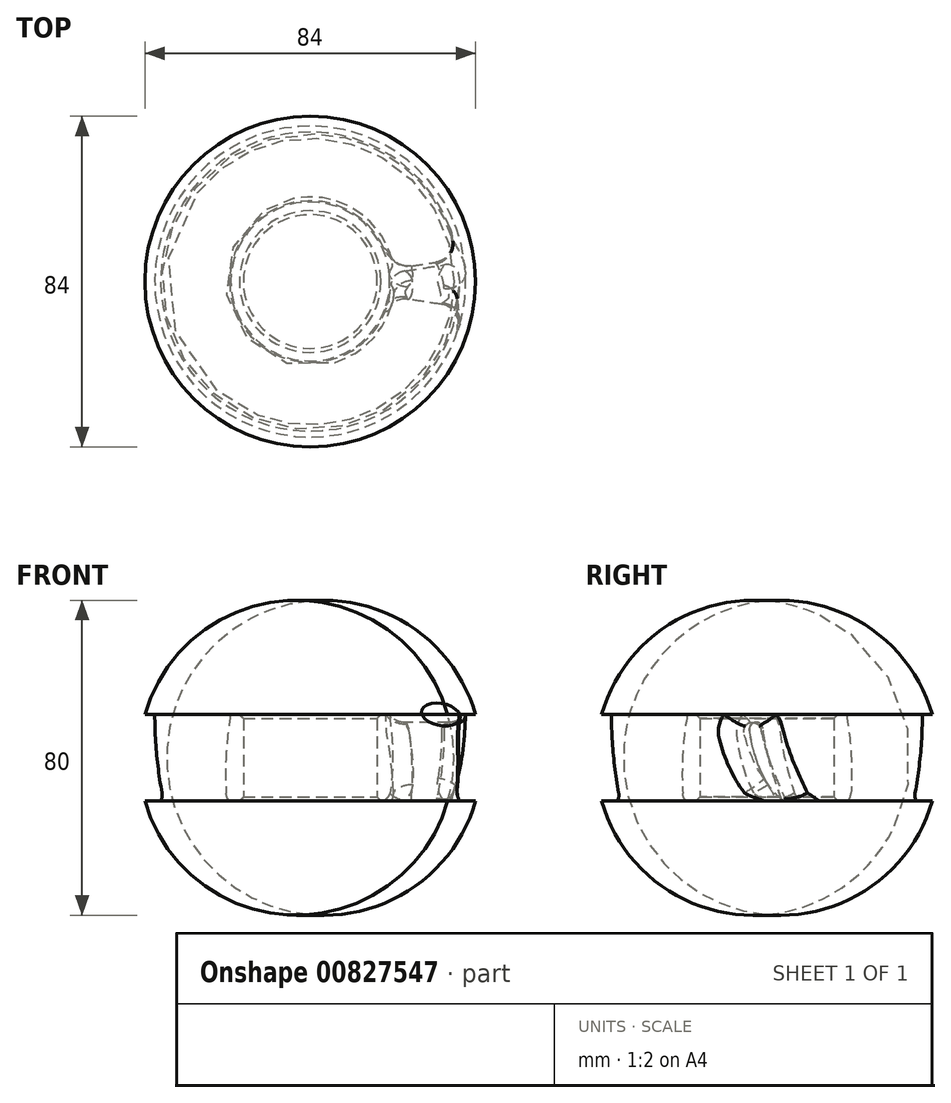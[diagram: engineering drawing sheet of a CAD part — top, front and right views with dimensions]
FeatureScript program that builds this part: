
annotation { "Feature Type Name" : "Feature", "Feature Type Description" : "" }
export const myFeature = defineFeature(function(context is Context, id is Id, definition is map)
    precondition{}
    {
        {
            var Q0;
            Q0=qCreatedBy(makeId("Right.planeOp"),FACE);
            cPlane(context, id + "F0", {"entities" : qUnion([Q0]), "cplaneType" : CPlaneType.OFFSET, "offset" : 20 * mm, "width" : 152.4 * mm, "height" : 152.4 * mm});
        }
        {
            var Q0;
            Q0=qCreatedBy(id+"F0.planeOp",FACE);
            cPlane(context, id + "F1", {"entities" : qUnion([Q0]), "cplaneType" : CPlaneType.OFFSET, "offset" : 10 * mm, "width" : 150 * mm, "height" : 150 * mm});
        }
        {
            var Q0;
            Q0=qCreatedBy(id+"F1.planeOp",FACE);
            cPlane(context, id + "F2", {"entities" : qUnion([Q0]), "cplaneType" : CPlaneType.OFFSET, "offset" : 10 * mm, "width" : 150 * mm, "height" : 150 * mm});
        }
        {
            var Q0;
            Q0=qCreatedBy(makeId("Right.planeOp"),FACE);
            var sketch = newSketch(context, id + "F3", { "sketchPlane" : qUnion([Q0])});
            skLineSegment(sketch, "E0.bottom", {"start": v(-22.5, 10) * mm, "end": v(22.5, 10) * mm});
            skLineSegment(sketch, "E0.top", {"start": v(-22.5, -10) * mm, "end": v(22.5, -10) * mm});
            skLineSegment(sketch, "E0.left", {"start": v(-22.5, 10) * mm, "end": v(-22.5, -10) * mm});
            skLineSegment(sketch, "E0.right", {"start": v(22.5, 10) * mm, "end": v(22.5, -10) * mm});
            skLineSegment(sketch, "E1", {"start": v(0, 10) * mm, "end": v(0, -10) * mm, "construction": true});
            skLineSegment(sketch, "E2", {"start": v(-22.5, 0) * mm, "end": v(22.5, 0) * mm, "construction": true});
            skSolve(sketch);
        }
        {
            var Q0;
            Q0=qCreatedBy(id+"F0.planeOp",FACE);
            var sketch = newSketch(context, id + "F4", { "sketchPlane" : qUnion([Q0])});
            skArc(sketch, "E3", {"start": v(-0.72, 8.68) * mm, "mid": v(-2.39, 9.99) * mm, "end": v(-3.7, 8.32) * mm});
            skArc(sketch, "E4", {"start": v(-0.72, 8.68) * mm, "mid": v(0.82, -0.73) * mm, "end": v(3.1, -10) * mm});
            skArc(sketch, "E5", {"start": v(-3.7, 8.32) * mm, "mid": v(-1.64, -1.1) * mm, "end": v(2.1, -10) * mm});
            skLineSegment(sketch, "E6", {"start": v(-3.7, 8.32) * mm, "end": v(-0.72, 8.68) * mm, "construction": true});
            skLineSegment(sketch, "E7", {"start": v(2.1, -10) * mm, "end": v(3.1, -10) * mm});
            skLineSegment(sketch, "E8", {"start": v(-2.2, 8.5) * mm, "end": v(2.6, -10) * mm, "construction": true});
            skLineSegment(sketch, "E9", {"start": v(48.43, 14.72) * mm, "end": v(2.1, -10) * mm, "construction": true});
            skLineSegment(sketch, "E10", {"start": v(119.1, 23.4) * mm, "end": v(3.1, -10) * mm, "construction": true});
            skSolve(sketch);
        }
        {
            var Q0;
            Q0=qCreatedBy(id+"F1.planeOp",FACE);
            var sketch = newSketch(context, id + "F5", { "sketchPlane" : qUnion([Q0])});
            skArc(sketch, "E11", {"start": v(-1.32, 8.36) * mm, "mid": v(-3.65, 9.97) * mm, "end": v(-5.26, 7.64) * mm});
            skArc(sketch, "E12", {"start": v(-5.26, 7.64) * mm, "mid": v(-2.08, -1.81) * mm, "end": v(3.61, -10) * mm});
            skArc(sketch, "E13", {"start": v(-1.32, 8.36) * mm, "mid": v(1.05, -1) * mm, "end": v(4.61, -10) * mm});
            skLineSegment(sketch, "E14", {"start": v(-3.29, 8) * mm, "end": v(4.11, -10) * mm, "construction": true});
            skLineSegment(sketch, "E15", {"start": v(-5.26, 7.64) * mm, "end": v(-1.32, 8.36) * mm, "construction": true});
            skLineSegment(sketch, "E16", {"start": v(3.61, -10) * mm, "end": v(4.61, -10) * mm});
            skLineSegment(sketch, "E17", {"start": v(29.55, 14.09) * mm, "end": v(3.61, -10) * mm, "construction": true});
            skLineSegment(sketch, "E18", {"start": v(72.3, 22) * mm, "end": v(4.61, -10) * mm, "construction": true});
            skSolve(sketch);
        }
        {
            var Q0;
            Q0=qCreatedBy(id+"F2.planeOp",FACE);
            var sketch = newSketch(context, id + "F6", { "sketchPlane" : qUnion([Q0])});
            skArc(sketch, "E19", {"start": v(-1.86, 8.1) * mm, "mid": v(-4.9, 9.93) * mm, "end": v(-6.71, 6.9) * mm});
            skArc(sketch, "E20", {"start": v(-6.71, 6.9) * mm, "mid": v(-2.33, -2.67) * mm, "end": v(5.21, -10) * mm});
            skArc(sketch, "E21", {"start": v(-1.86, 8.1) * mm, "mid": v(1.38, -1.3) * mm, "end": v(6.21, -10) * mm});
            skLineSegment(sketch, "E22", {"start": v(5.21, -10) * mm, "end": v(6.21, -10) * mm});
            skLineSegment(sketch, "E23", {"start": v(-6.71, 6.9) * mm, "end": v(-1.86, 8.1) * mm, "construction": true});
            skLineSegment(sketch, "E24", {"start": v(21.01, 13.8) * mm, "end": v(5.21, -10) * mm, "construction": true});
            skLineSegment(sketch, "E25", {"start": v(-4.29, 7.5) * mm, "end": v(5.71, -10) * mm, "construction": true});
            skLineSegment(sketch, "E26", {"start": v(6.21, -10) * mm, "end": v(53.33, 21.87) * mm, "construction": true});
            skSolve(sketch);
        }
        {
            var Q0;
            Q0 = qSketchRegion(id + "F4", true);
            var Q1;
            Q1 = qSketchRegion(id + "F5", true);
            var Q2;
            Q2 = qSketchRegion(id + "F6", true);
            loft(context, id + "F7", {"sheetProfilesArray" : [{ "sheetProfileEntities" : qUnion([Q0]) }, { "sheetProfileEntities" : qUnion([Q1]) }, { "sheetProfileEntities" : qUnion([Q2]) }]});
        }
        {
            var Q0;
            Q0=qCreatedBy(makeId("Front.planeOp"),FACE);
            var sketch = newSketch(context, id + "F8", { "sketchPlane" : qUnion([Q0])});
            skLineSegment(sketch, "E27", {"start": v(0, 0) * mm, "end": v(0, 20) * mm, "construction": true});
            skLineSegment(sketch, "E28", {"start": v(17, -10) * mm, "end": v(17, 11.99) * mm});
            skLineSegment(sketch, "E29", {"start": v(17, 11.99) * mm, "end": v(20.2, 11.99) * mm});
            skLineSegment(sketch, "E30", {"start": v(20.5, -10) * mm, "end": v(17, -10) * mm});
            skLineSegment(sketch, "E31", {"start": v(42, 11.99) * mm, "end": v(42, -10) * mm, "construction": true});
            skLineSegment(sketch, "E32", {"start": v(42, -10) * mm, "end": v(38, -10) * mm});
            skLineSegment(sketch, "E33", {"start": v(39.5, 11.99) * mm, "end": v(42, 11.99) * mm});
            skArc(sketch, "E34", {"start": v(42, -10) * mm, "mid": v(43.54, 1) * mm, "end": v(42, 11.99) * mm});
            skArc(sketch, "E35", {"start": v(20.5, -10) * mm, "mid": v(21.12, -9.1) * mm, "end": v(21.37, -8.05) * mm});
            skArc(sketch, "E36", {"start": v(20.2, 11.99) * mm, "mid": v(21.37, 2) * mm, "end": v(21.37, -8.05) * mm});
            skLineSegment(sketch, "E37", {"start": v(18.38, -7.88) * mm, "end": v(20.5, -10) * mm, "construction": true});
            skArc(sketch, "E38", {"start": v(37.65, -7.95) * mm, "mid": v(39.04, 1.98) * mm, "end": v(39.5, 11.99) * mm});
            skArc(sketch, "E39", {"start": v(37.65, -7.95) * mm, "mid": v(37.64, -9) * mm, "end": v(38, -10) * mm});
            skLineSegment(sketch, "E40", {"start": v(40.6, -8.5) * mm, "end": v(38, -10) * mm, "construction": true});
            skLineSegment(sketch, "E41", {"start": v(-65.18, -3.07) * mm, "end": v(20.2, 11.99) * mm, "construction": true});
            skSolve(sketch);
        }
        {
            var Q0;
            Q0=makeQuery(id+"F8.imprint","IMPRINT",FACE,{"disambiguationData":[TD([[makeQuery(id+"F8.imprint","IMPRINT",EDGE,{"derivedFrom":sQuery(id+"F8.wireOp",EDGE,"E28")}),-1.0]])]});
            var Q1;
            Q1=sQuery(id+"F8.wireOp",EDGE,"E27");
            revolve(context, id + "F9", {"operationType" : NewBodyOperationType.ADD, "surfaceOperationType" : NewSurfaceOperationType.NEW, "entities" : qUnion([Q0]), "axis" : qUnion([Q1]), "revolveType" : RevolveType.FULL});
        }
        {
            var Q0;
            Q0=makeQuery(id+"F8.imprint","IMPRINT",FACE,{"disambiguationData":[TD([[makeQuery(id+"F8.imprint","IMPRINT",EDGE,{"derivedFrom":sQuery(id+"F8.wireOp",EDGE,"E32")}),-1.0]])]});
            var Q1;
            Q1=sQuery(id+"F8.wireOp",EDGE,"E27");
            revolve(context, id + "F10", {"operationType" : NewBodyOperationType.ADD, "surfaceOperationType" : NewSurfaceOperationType.NEW, "entities" : qUnion([Q0]), "axis" : qUnion([Q1]), "revolveType" : RevolveType.FULL});
        }
        {
            var Q0;
            Q0=makeQuery(id+"F9.boolean.opBoolean","INTERSECT",EDGE,{"derivedFrom":[makeQuery(id+"F7.opLoft","SWEPT_FACE",FACE,{"disambiguationData":[OSD([sQuery(id+"F4.wireOp",EDGE,"E3"),sQuery(id+"F4.wireOp",EDGE,"E4"),sQuery(id+"F4.wireOp",EDGE,"E7"),sQuery(id+"F5.wireOp",EDGE,"E11"),sQuery(id+"F5.wireOp",EDGE,"E13"),sQuery(id+"F5.wireOp",EDGE,"E16")])]}),makeQuery(id+"F9.opRevolve","SWEPT_FACE",FACE,{"disambiguationData":[OSD([sQuery(id+"F8.wireOp",EDGE,"E36")])]})]});
            var Q1;
            Q1=makeQuery(id+"F9.boolean.opBoolean","INTERSECT",EDGE,{"derivedFrom":[makeQuery(id+"F53g4K2dghI7kLQ_1.1.F7.opLoft","SWEPT_FACE",FACE,{"disambiguationData":[OSD([sQuery(id+"F4.wireOp",EDGE,"E3"),sQuery(id+"F4.wireOp",EDGE,"E4"),sQuery(id+"F4.wireOp",EDGE,"E7"),sQuery(id+"F5.wireOp",EDGE,"E11"),sQuery(id+"F5.wireOp",EDGE,"E13"),sQuery(id+"F5.wireOp",EDGE,"E16")])]}),makeQuery(id+"F9.opRevolve","SWEPT_FACE",FACE,{"disambiguationData":[OSD([sQuery(id+"F8.wireOp",EDGE,"E36")])]})]});
            var Q2;
            Q2=makeQuery(id+"F9.boolean.opBoolean","INTERSECT",EDGE,{"derivedFrom":[makeQuery(id+"F53g4K2dghI7kLQ_1.2.F7.opLoft","SWEPT_FACE",FACE,{"disambiguationData":[OSD([sQuery(id+"F4.wireOp",EDGE,"E3"),sQuery(id+"F4.wireOp",EDGE,"E4"),sQuery(id+"F4.wireOp",EDGE,"E7"),sQuery(id+"F5.wireOp",EDGE,"E11"),sQuery(id+"F5.wireOp",EDGE,"E13"),sQuery(id+"F5.wireOp",EDGE,"E16")])]}),makeQuery(id+"F9.opRevolve","SWEPT_FACE",FACE,{"disambiguationData":[OSD([sQuery(id+"F8.wireOp",EDGE,"E36")])]})]});
            var Q3;
            Q3=makeQuery(id+"F9.boolean.opBoolean","INTERSECT",EDGE,{"derivedFrom":[makeQuery(id+"F53g4K2dghI7kLQ_1.3.F7.opLoft","SWEPT_FACE",FACE,{"disambiguationData":[OSD([sQuery(id+"F4.wireOp",EDGE,"E3"),sQuery(id+"F4.wireOp",EDGE,"E4"),sQuery(id+"F4.wireOp",EDGE,"E7"),sQuery(id+"F5.wireOp",EDGE,"E11"),sQuery(id+"F5.wireOp",EDGE,"E13"),sQuery(id+"F5.wireOp",EDGE,"E16")])]}),makeQuery(id+"F9.opRevolve","SWEPT_FACE",FACE,{"disambiguationData":[OSD([sQuery(id+"F8.wireOp",EDGE,"E36")])]})]});
            var Q4;
            Q4=makeQuery(id+"F9.boolean.opBoolean","INTERSECT",EDGE,{"derivedFrom":[makeQuery(id+"F53g4K2dghI7kLQ_1.4.F7.opLoft","SWEPT_FACE",FACE,{"disambiguationData":[OSD([sQuery(id+"F4.wireOp",EDGE,"E3"),sQuery(id+"F4.wireOp",EDGE,"E4"),sQuery(id+"F4.wireOp",EDGE,"E7"),sQuery(id+"F5.wireOp",EDGE,"E11"),sQuery(id+"F5.wireOp",EDGE,"E13"),sQuery(id+"F5.wireOp",EDGE,"E16")])]}),makeQuery(id+"F9.opRevolve","SWEPT_FACE",FACE,{"disambiguationData":[OSD([sQuery(id+"F8.wireOp",EDGE,"E36")])]})]});
            var Q5;
            Q5=makeQuery(id+"F9.boolean.opBoolean","INTERSECT",EDGE,{"derivedFrom":[makeQuery(id+"F53g4K2dghI7kLQ_1.5.F7.opLoft","SWEPT_FACE",FACE,{"disambiguationData":[OSD([sQuery(id+"F4.wireOp",EDGE,"E3"),sQuery(id+"F4.wireOp",EDGE,"E4"),sQuery(id+"F4.wireOp",EDGE,"E7"),sQuery(id+"F5.wireOp",EDGE,"E11"),sQuery(id+"F5.wireOp",EDGE,"E13"),sQuery(id+"F5.wireOp",EDGE,"E16")])]}),makeQuery(id+"F9.opRevolve","SWEPT_FACE",FACE,{"disambiguationData":[OSD([sQuery(id+"F8.wireOp",EDGE,"E36")])]})]});
            var Q6;
            Q6=makeQuery(id+"F9.boolean.opBoolean","INTERSECT",EDGE,{"derivedFrom":[makeQuery(id+"F53g4K2dghI7kLQ_1.6.F7.opLoft","SWEPT_FACE",FACE,{"disambiguationData":[OSD([sQuery(id+"F4.wireOp",EDGE,"E3"),sQuery(id+"F4.wireOp",EDGE,"E4"),sQuery(id+"F4.wireOp",EDGE,"E7"),sQuery(id+"F5.wireOp",EDGE,"E11"),sQuery(id+"F5.wireOp",EDGE,"E13"),sQuery(id+"F5.wireOp",EDGE,"E16")])]}),makeQuery(id+"F9.opRevolve","SWEPT_FACE",FACE,{"disambiguationData":[OSD([sQuery(id+"F8.wireOp",EDGE,"E36")])]})]});
            var Q7;
            Q7=makeQuery(id+"F9.boolean.opBoolean","INTERSECT",EDGE,{"derivedFrom":[makeQuery(id+"F53g4K2dghI7kLQ_1.7.F7.opLoft","SWEPT_FACE",FACE,{"disambiguationData":[OSD([sQuery(id+"F4.wireOp",EDGE,"E3"),sQuery(id+"F4.wireOp",EDGE,"E4"),sQuery(id+"F4.wireOp",EDGE,"E7"),sQuery(id+"F5.wireOp",EDGE,"E11"),sQuery(id+"F5.wireOp",EDGE,"E13"),sQuery(id+"F5.wireOp",EDGE,"E16")])]}),makeQuery(id+"F9.opRevolve","SWEPT_FACE",FACE,{"disambiguationData":[OSD([sQuery(id+"F8.wireOp",EDGE,"E36")])]})]});
            var Q8;
            Q8=makeQuery(id+"F9.boolean.opBoolean","INTERSECT",EDGE,{"derivedFrom":[makeQuery(id+"F53g4K2dghI7kLQ_1.8.F7.opLoft","SWEPT_FACE",FACE,{"disambiguationData":[OSD([sQuery(id+"F4.wireOp",EDGE,"E3"),sQuery(id+"F4.wireOp",EDGE,"E4"),sQuery(id+"F4.wireOp",EDGE,"E7"),sQuery(id+"F5.wireOp",EDGE,"E11"),sQuery(id+"F5.wireOp",EDGE,"E13"),sQuery(id+"F5.wireOp",EDGE,"E16")])]}),makeQuery(id+"F9.opRevolve","SWEPT_FACE",FACE,{"disambiguationData":[OSD([sQuery(id+"F8.wireOp",EDGE,"E36")])]})]});
            var Q9;
            Q9=makeQuery(id+"F9.boolean.opBoolean","INTERSECT",EDGE,{"derivedFrom":[makeQuery(id+"F53g4K2dghI7kLQ_1.9.F7.opLoft","SWEPT_FACE",FACE,{"disambiguationData":[OSD([sQuery(id+"F4.wireOp",EDGE,"E3"),sQuery(id+"F4.wireOp",EDGE,"E4"),sQuery(id+"F4.wireOp",EDGE,"E7"),sQuery(id+"F5.wireOp",EDGE,"E11"),sQuery(id+"F5.wireOp",EDGE,"E13"),sQuery(id+"F5.wireOp",EDGE,"E16")])]}),makeQuery(id+"F9.opRevolve","SWEPT_FACE",FACE,{"disambiguationData":[OSD([sQuery(id+"F8.wireOp",EDGE,"E36")])]})]});
            var Q10;
            Q10=makeQuery(id+"F9.boolean.opBoolean","INTERSECT",EDGE,{"derivedFrom":[makeQuery(id+"F53g4K2dghI7kLQ_1.10.F7.opLoft","SWEPT_FACE",FACE,{"disambiguationData":[OSD([sQuery(id+"F4.wireOp",EDGE,"E3"),sQuery(id+"F4.wireOp",EDGE,"E4"),sQuery(id+"F4.wireOp",EDGE,"E7"),sQuery(id+"F5.wireOp",EDGE,"E11"),sQuery(id+"F5.wireOp",EDGE,"E13"),sQuery(id+"F5.wireOp",EDGE,"E16")])]}),makeQuery(id+"F9.opRevolve","SWEPT_FACE",FACE,{"disambiguationData":[OSD([sQuery(id+"F8.wireOp",EDGE,"E36")])]})]});
            var Q11;
            Q11=makeQuery(id+"F9.boolean.opBoolean","INTERSECT",EDGE,{"derivedFrom":[makeQuery(id+"F53g4K2dghI7kLQ_1.11.F7.opLoft","SWEPT_FACE",FACE,{"disambiguationData":[OSD([sQuery(id+"F4.wireOp",EDGE,"E3"),sQuery(id+"F4.wireOp",EDGE,"E4"),sQuery(id+"F4.wireOp",EDGE,"E7"),sQuery(id+"F5.wireOp",EDGE,"E11"),sQuery(id+"F5.wireOp",EDGE,"E13"),sQuery(id+"F5.wireOp",EDGE,"E16")])]}),makeQuery(id+"F9.opRevolve","SWEPT_FACE",FACE,{"disambiguationData":[OSD([sQuery(id+"F8.wireOp",EDGE,"E36")])]})]});
            var Q12;
            Q12=makeQuery(id+"F9.boolean.opBoolean","INTERSECT",EDGE,{"derivedFrom":[makeQuery(id+"F53g4K2dghI7kLQ_1.12.F7.opLoft","SWEPT_FACE",FACE,{"disambiguationData":[OSD([sQuery(id+"F4.wireOp",EDGE,"E3"),sQuery(id+"F4.wireOp",EDGE,"E4"),sQuery(id+"F4.wireOp",EDGE,"E7"),sQuery(id+"F5.wireOp",EDGE,"E11"),sQuery(id+"F5.wireOp",EDGE,"E13"),sQuery(id+"F5.wireOp",EDGE,"E16")])]}),makeQuery(id+"F9.opRevolve","SWEPT_FACE",FACE,{"disambiguationData":[OSD([sQuery(id+"F8.wireOp",EDGE,"E36")])]})]});
            var Q13;
            Q13=makeQuery(id+"F9.boolean.opBoolean","INTERSECT",EDGE,{"derivedFrom":[makeQuery(id+"F53g4K2dghI7kLQ_1.13.F7.opLoft","SWEPT_FACE",FACE,{"disambiguationData":[OSD([sQuery(id+"F4.wireOp",EDGE,"E3"),sQuery(id+"F4.wireOp",EDGE,"E4"),sQuery(id+"F4.wireOp",EDGE,"E7"),sQuery(id+"F5.wireOp",EDGE,"E11"),sQuery(id+"F5.wireOp",EDGE,"E13"),sQuery(id+"F5.wireOp",EDGE,"E16")])]}),makeQuery(id+"F9.opRevolve","SWEPT_FACE",FACE,{"disambiguationData":[OSD([sQuery(id+"F8.wireOp",EDGE,"E36")])]})]});
            var Q14;
            Q14=makeQuery(id+"F9.boolean.opBoolean","INTERSECT",EDGE,{"derivedFrom":[makeQuery(id+"F53g4K2dghI7kLQ_1.14.F7.opLoft","SWEPT_FACE",FACE,{"disambiguationData":[OSD([sQuery(id+"F4.wireOp",EDGE,"E3"),sQuery(id+"F4.wireOp",EDGE,"E4"),sQuery(id+"F4.wireOp",EDGE,"E7"),sQuery(id+"F5.wireOp",EDGE,"E11"),sQuery(id+"F5.wireOp",EDGE,"E13"),sQuery(id+"F5.wireOp",EDGE,"E16")])]}),makeQuery(id+"F9.opRevolve","SWEPT_FACE",FACE,{"disambiguationData":[OSD([sQuery(id+"F8.wireOp",EDGE,"E36")])]})]});
            var Q15;
            Q15=makeQuery(id+"F10.boolean.opBoolean","INTERSECT",EDGE,{"derivedFrom":[makeQuery(id+"F7.opLoft","SWEPT_FACE",FACE,{"disambiguationData":[OSD([sQuery(id+"F4.wireOp",EDGE,"E3"),sQuery(id+"F4.wireOp",EDGE,"E4"),sQuery(id+"F4.wireOp",EDGE,"E7"),sQuery(id+"F5.wireOp",EDGE,"E11"),sQuery(id+"F5.wireOp",EDGE,"E13"),sQuery(id+"F5.wireOp",EDGE,"E16")])]}),makeQuery(id+"F10.opRevolve","SWEPT_FACE",FACE,{"disambiguationData":[OSD([sQuery(id+"F8.wireOp",EDGE,"E38")])]})]});
            var Q16;
            Q16=makeQuery(id+"F10.boolean.opBoolean","INTERSECT",EDGE,{"derivedFrom":[makeQuery(id+"F53g4K2dghI7kLQ_1.1.F7.opLoft","SWEPT_FACE",FACE,{"disambiguationData":[OSD([sQuery(id+"F4.wireOp",EDGE,"E3"),sQuery(id+"F4.wireOp",EDGE,"E4"),sQuery(id+"F4.wireOp",EDGE,"E7"),sQuery(id+"F5.wireOp",EDGE,"E11"),sQuery(id+"F5.wireOp",EDGE,"E13"),sQuery(id+"F5.wireOp",EDGE,"E16")])]}),makeQuery(id+"F10.opRevolve","SWEPT_FACE",FACE,{"disambiguationData":[OSD([sQuery(id+"F8.wireOp",EDGE,"E38")])]})]});
            var Q17;
            Q17=makeQuery(id+"F10.boolean.opBoolean","INTERSECT",EDGE,{"derivedFrom":[makeQuery(id+"F53g4K2dghI7kLQ_1.2.F7.opLoft","SWEPT_FACE",FACE,{"disambiguationData":[OSD([sQuery(id+"F4.wireOp",EDGE,"E3"),sQuery(id+"F4.wireOp",EDGE,"E4"),sQuery(id+"F4.wireOp",EDGE,"E7"),sQuery(id+"F5.wireOp",EDGE,"E11"),sQuery(id+"F5.wireOp",EDGE,"E13"),sQuery(id+"F5.wireOp",EDGE,"E16")])]}),makeQuery(id+"F10.opRevolve","SWEPT_FACE",FACE,{"disambiguationData":[OSD([sQuery(id+"F8.wireOp",EDGE,"E38")])]})]});
            var Q18;
            Q18=makeQuery(id+"F10.boolean.opBoolean","INTERSECT",EDGE,{"derivedFrom":[makeQuery(id+"F53g4K2dghI7kLQ_1.3.F7.opLoft","SWEPT_FACE",FACE,{"disambiguationData":[OSD([sQuery(id+"F4.wireOp",EDGE,"E3"),sQuery(id+"F4.wireOp",EDGE,"E4"),sQuery(id+"F4.wireOp",EDGE,"E7"),sQuery(id+"F5.wireOp",EDGE,"E11"),sQuery(id+"F5.wireOp",EDGE,"E13"),sQuery(id+"F5.wireOp",EDGE,"E16")])]}),makeQuery(id+"F10.opRevolve","SWEPT_FACE",FACE,{"disambiguationData":[OSD([sQuery(id+"F8.wireOp",EDGE,"E38")])]})]});
            var Q19;
            Q19=makeQuery(id+"F10.boolean.opBoolean","INTERSECT",EDGE,{"derivedFrom":[makeQuery(id+"F53g4K2dghI7kLQ_1.4.F7.opLoft","SWEPT_FACE",FACE,{"disambiguationData":[OSD([sQuery(id+"F4.wireOp",EDGE,"E3"),sQuery(id+"F4.wireOp",EDGE,"E4"),sQuery(id+"F4.wireOp",EDGE,"E7"),sQuery(id+"F5.wireOp",EDGE,"E11"),sQuery(id+"F5.wireOp",EDGE,"E13"),sQuery(id+"F5.wireOp",EDGE,"E16")])]}),makeQuery(id+"F10.opRevolve","SWEPT_FACE",FACE,{"disambiguationData":[OSD([sQuery(id+"F8.wireOp",EDGE,"E38")])]})]});
            var Q20;
            Q20=makeQuery(id+"F10.boolean.opBoolean","INTERSECT",EDGE,{"derivedFrom":[makeQuery(id+"F53g4K2dghI7kLQ_1.5.F7.opLoft","SWEPT_FACE",FACE,{"disambiguationData":[OSD([sQuery(id+"F4.wireOp",EDGE,"E3"),sQuery(id+"F4.wireOp",EDGE,"E4"),sQuery(id+"F4.wireOp",EDGE,"E7"),sQuery(id+"F5.wireOp",EDGE,"E11"),sQuery(id+"F5.wireOp",EDGE,"E13"),sQuery(id+"F5.wireOp",EDGE,"E16")])]}),makeQuery(id+"F10.opRevolve","SWEPT_FACE",FACE,{"disambiguationData":[OSD([sQuery(id+"F8.wireOp",EDGE,"E38")])]})]});
            var Q21;
            Q21=makeQuery(id+"F10.boolean.opBoolean","INTERSECT",EDGE,{"derivedFrom":[makeQuery(id+"F53g4K2dghI7kLQ_1.6.F7.opLoft","SWEPT_FACE",FACE,{"disambiguationData":[OSD([sQuery(id+"F4.wireOp",EDGE,"E3"),sQuery(id+"F4.wireOp",EDGE,"E4"),sQuery(id+"F4.wireOp",EDGE,"E7"),sQuery(id+"F5.wireOp",EDGE,"E11"),sQuery(id+"F5.wireOp",EDGE,"E13"),sQuery(id+"F5.wireOp",EDGE,"E16")])]}),makeQuery(id+"F10.opRevolve","SWEPT_FACE",FACE,{"disambiguationData":[OSD([sQuery(id+"F8.wireOp",EDGE,"E38")])]})]});
            var Q22;
            Q22=makeQuery(id+"F10.boolean.opBoolean","INTERSECT",EDGE,{"derivedFrom":[makeQuery(id+"F53g4K2dghI7kLQ_1.7.F7.opLoft","SWEPT_FACE",FACE,{"disambiguationData":[OSD([sQuery(id+"F4.wireOp",EDGE,"E3"),sQuery(id+"F4.wireOp",EDGE,"E4"),sQuery(id+"F4.wireOp",EDGE,"E7"),sQuery(id+"F5.wireOp",EDGE,"E11"),sQuery(id+"F5.wireOp",EDGE,"E13"),sQuery(id+"F5.wireOp",EDGE,"E16")])]}),makeQuery(id+"F10.opRevolve","SWEPT_FACE",FACE,{"disambiguationData":[OSD([sQuery(id+"F8.wireOp",EDGE,"E38")])]})]});
            var Q23;
            Q23=makeQuery(id+"F10.boolean.opBoolean","INTERSECT",EDGE,{"derivedFrom":[makeQuery(id+"F53g4K2dghI7kLQ_1.8.F7.opLoft","SWEPT_FACE",FACE,{"disambiguationData":[OSD([sQuery(id+"F4.wireOp",EDGE,"E3"),sQuery(id+"F4.wireOp",EDGE,"E4"),sQuery(id+"F4.wireOp",EDGE,"E7"),sQuery(id+"F5.wireOp",EDGE,"E11"),sQuery(id+"F5.wireOp",EDGE,"E13"),sQuery(id+"F5.wireOp",EDGE,"E16")])]}),makeQuery(id+"F10.opRevolve","SWEPT_FACE",FACE,{"disambiguationData":[OSD([sQuery(id+"F8.wireOp",EDGE,"E38")])]})]});
            var Q24;
            Q24=makeQuery(id+"F10.boolean.opBoolean","INTERSECT",EDGE,{"derivedFrom":[makeQuery(id+"F53g4K2dghI7kLQ_1.9.F7.opLoft","SWEPT_FACE",FACE,{"disambiguationData":[OSD([sQuery(id+"F4.wireOp",EDGE,"E3"),sQuery(id+"F4.wireOp",EDGE,"E4"),sQuery(id+"F4.wireOp",EDGE,"E7"),sQuery(id+"F5.wireOp",EDGE,"E11"),sQuery(id+"F5.wireOp",EDGE,"E13"),sQuery(id+"F5.wireOp",EDGE,"E16")])]}),makeQuery(id+"F10.opRevolve","SWEPT_FACE",FACE,{"disambiguationData":[OSD([sQuery(id+"F8.wireOp",EDGE,"E38")])]})]});
            var Q25;
            Q25=makeQuery(id+"F10.boolean.opBoolean","INTERSECT",EDGE,{"derivedFrom":[makeQuery(id+"F53g4K2dghI7kLQ_1.10.F7.opLoft","SWEPT_FACE",FACE,{"disambiguationData":[OSD([sQuery(id+"F4.wireOp",EDGE,"E3"),sQuery(id+"F4.wireOp",EDGE,"E4"),sQuery(id+"F4.wireOp",EDGE,"E7"),sQuery(id+"F5.wireOp",EDGE,"E11"),sQuery(id+"F5.wireOp",EDGE,"E13"),sQuery(id+"F5.wireOp",EDGE,"E16")])]}),makeQuery(id+"F10.opRevolve","SWEPT_FACE",FACE,{"disambiguationData":[OSD([sQuery(id+"F8.wireOp",EDGE,"E38")])]})]});
            fillet(context, id + "F11", {"entities" : qUnion([Q0, Q1, Q2, Q3, Q4, Q5, Q6, Q7, Q8, Q9, Q10, Q11, Q12, Q13, Q14, Q15, Q16, Q17, Q18, Q19, Q20, Q21, Q22, Q23, Q24, Q25]), "radius" : 5 * mm, "tangentPropagation" : true, "allowEdgeOverflow" : false});
        }
        {
            var Q0;
            Q0=makeQuery(id+"F9.opRevolve","SWEPT_FACE",FACE,{"disambiguationData":[OSD([sQuery(id+"F8.wireOp",EDGE,"E28")])]});
            chamfer(context, id + "F12", {"entities" : qUnion([Q0]), "width" : 1 * mm, "tangentPropagation" : true});
        }
    });
